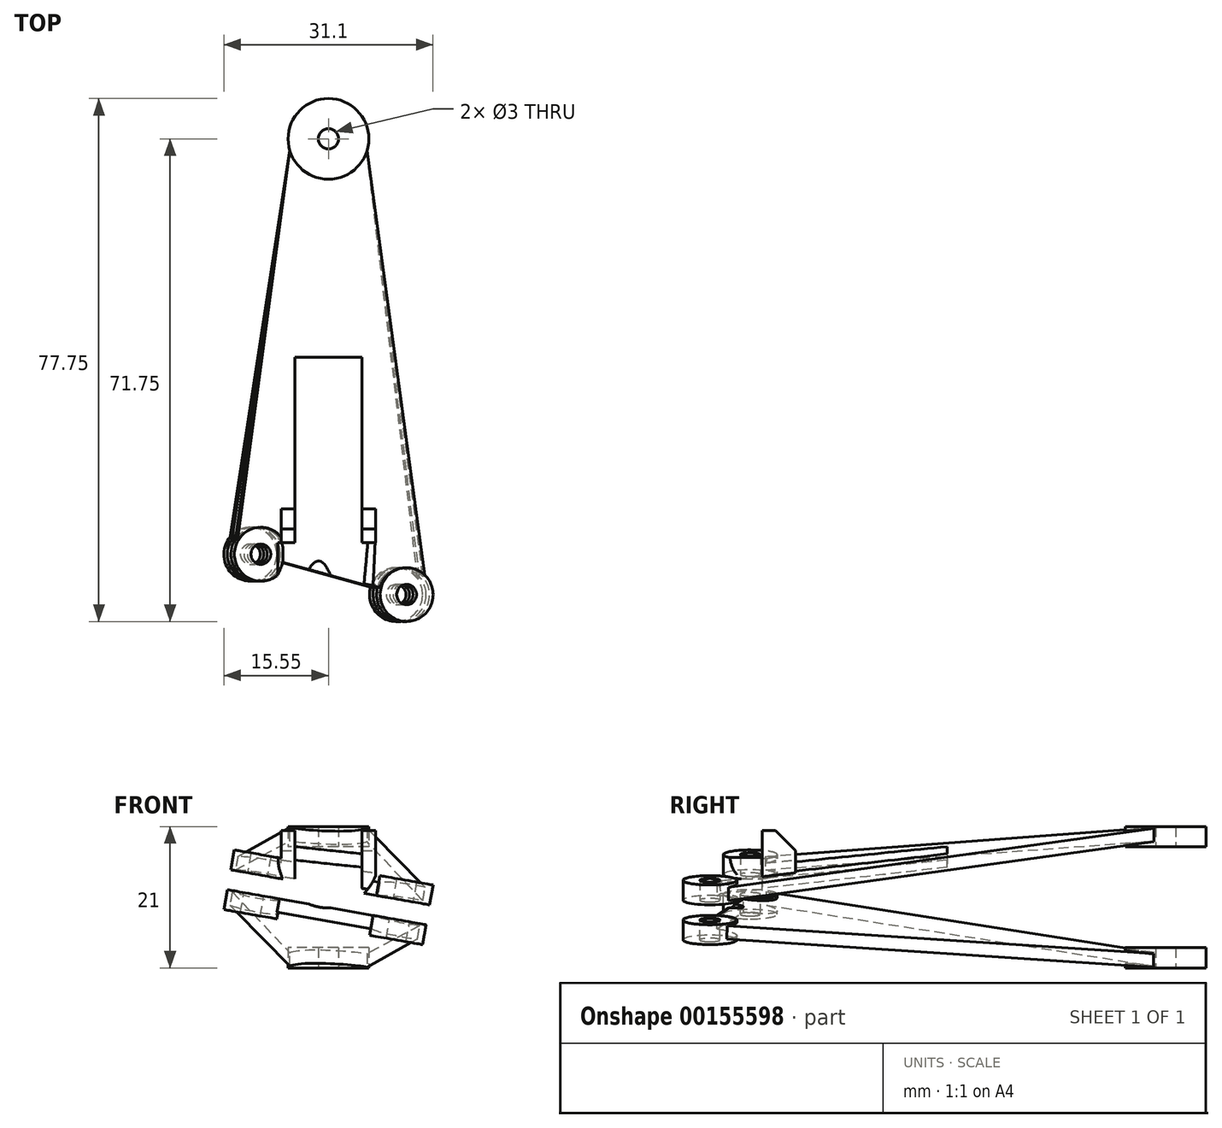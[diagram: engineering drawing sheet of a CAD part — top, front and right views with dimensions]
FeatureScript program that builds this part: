
annotation { "Feature Type Name" : "Feature", "Feature Type Description" : "" }
export const myFeature = defineFeature(function(context is Context, id is Id, definition is map)
    precondition{}
    {
        {
            var Q0;
            Q0=qCreatedBy(makeId("Front.planeOp"),FACE);
            var sketch = newSketch(context, id + "F0", { "sketchPlane" : qUnion([Q0])});
            skLineSegment(sketch, "E0", {"start": v(0, 0) * mm, "end": v(1.04, 5.9) * mm});
            skCircle(sketch, "E1", {"center": v(1.04, 5.9) * mm, "radius": 6 * mm});
            skLineSegment(sketch, "E2", {"start": v(0, 0) * mm, "end": v(-15.76, 2.78) * mm});
            skLineSegment(sketch, "E3", {"start": v(0, 0) * mm, "end": v(15.76, -2.78) * mm});
            skLineSegment(sketch, "E4", {"start": v(-10.83, 1.91) * mm, "end": v(-10.57, 3.39) * mm});
            skLineSegment(sketch, "E5", {"start": v(10.83, -1.91) * mm, "end": v(11.1, -0.43) * mm});
            skLineSegment(sketch, "E6", {"start": v(-10.83, 1.91) * mm, "end": v(-11.1, 0.43) * mm});
            skLineSegment(sketch, "E7", {"start": v(10.83, -1.91) * mm, "end": v(10.57, -3.39) * mm});
            skLineSegment(sketch, "E8", {"start": v(-5.9, 1.04) * mm, "end": v(-5.65, 2.52) * mm});
            skLineSegment(sketch, "E9", {"start": v(5.9, -1.04) * mm, "end": v(6.17, 0.44) * mm});
            skLineSegment(sketch, "E10", {"start": v(-5.9, 1.04) * mm, "end": v(-6.17, -0.44) * mm});
            skLineSegment(sketch, "E11", {"start": v(5.9, -1.04) * mm, "end": v(5.65, -2.52) * mm});
            skLineSegment(sketch, "E12.bottom", {"start": v(-10, 7.5) * mm, "end": v(10, 7.5) * mm});
            skLineSegment(sketch, "E12.top", {"start": v(-10, -7.5) * mm, "end": v(10, -7.5) * mm});
            skLineSegment(sketch, "E12.left", {"start": v(-10, 7.5) * mm, "end": v(-10, -7.5) * mm});
            skLineSegment(sketch, "E12.right", {"start": v(10, 7.5) * mm, "end": v(10, -7.5) * mm});
            skLineSegment(sketch, "E13", {"start": v(-9.5, -5.75) * mm, "end": v(9.5, -5.75) * mm});
            skLineSegment(sketch, "E14", {"start": v(-9.5, -3) * mm, "end": v(9.5, -3) * mm});
            skLineSegment(sketch, "E15", {"start": v(-9.5, 3) * mm, "end": v(9.5, 3) * mm});
            skLineSegment(sketch, "E16", {"start": v(-9.5, 5.75) * mm, "end": v(9.5, 5.75) * mm});
            skLineSegment(sketch, "E17", {"start": v(9.5, 7.5) * mm, "end": v(9.5, -7.5) * mm});
            skLineSegment(sketch, "E18", {"start": v(-9.5, 7.5) * mm, "end": v(-9.5, -7.5) * mm});
            skPoint(sketch, "E19.orphan", {"position": v(10, 5.75) * mm});
            skPoint(sketch, "E20.orphan", {"position": v(10, 3) * mm});
            skPoint(sketch, "E21.orphan", {"position": v(10, -3) * mm});
            skPoint(sketch, "E22.orphan", {"position": v(10, -5.75) * mm});
            skLineSegment(sketch, "E23", {"start": v(0, 7.5) * mm, "end": v(0, -7.5) * mm});
            skSolve(sketch);
        }
        {
            var Q0;
            {var subQ0=sQuery(id+"F0.wireOp",EDGE,"E12.bottom");var subQ1=sQuery(id+"F0.wireOp",EDGE,"E1");var subQ2=makeQuery(id+"F0.imprint","INTERSECT",VERTEX,{"disambiguationData":[OD(0.0)],"derivedFrom":[subQ1,subQ0]});Q0=makeQuery(id+"F0.imprint","IMPRINT",FACE,{"disambiguationData":[TD([[makeQuery(id+"F0.imprint","IMPRINT",EDGE,{"disambiguationData":[TD([[subQ2,1.0]])],"derivedFrom":subQ1}),1.0]])]});}
            cPlane(context, id + "F1", {"entities" : qUnion([Q0]), "cplaneType" : CPlaneType.OFFSET, "offset" : 1.75 * mm, "width" : 150 * mm, "height" : 150 * mm});
        }
        {
            var Q0;
            Q0=qCreatedBy(id+"F1.planeOp",FACE);
            var sketch = newSketch(context, id + "F2", { "sketchPlane" : qUnion([Q0])});
            skLineSegment(sketch, "E24", {"start": v(0, 0) * mm, "end": v(-10.83, 1.91) * mm});
            skLineSegment(sketch, "E25", {"start": v(-10.83, 1.91) * mm, "end": v(-10.05, 6.34) * mm});
            skSolve(sketch);
        }
        {
            var Q0;
            {var subQ0=sQuery(id+"F0.wireOp",EDGE,"E12.bottom");var subQ1=sQuery(id+"F0.wireOp",EDGE,"E1");var subQ2=makeQuery(id+"F0.imprint","INTERSECT",VERTEX,{"disambiguationData":[OD(0.0)],"derivedFrom":[subQ1,subQ0]});Q0=makeQuery(id+"F0.imprint","IMPRINT",FACE,{"disambiguationData":[TD([[makeQuery(id+"F0.imprint","IMPRINT",EDGE,{"disambiguationData":[TD([[subQ2,1.0]])],"derivedFrom":subQ1}),1.0]])]});}
            cPlane(context, id + "F3", {"entities" : qUnion([Q0]), "cplaneType" : CPlaneType.OFFSET, "offset" : 7.75 * mm, "width" : 150 * mm, "height" : 150 * mm});
        }
        {
            var Q0;
            Q0=qCreatedBy(id+"F3.planeOp",FACE);
            var sketch = newSketch(context, id + "F4", { "sketchPlane" : qUnion([Q0])});
            skLineSegment(sketch, "E26", {"start": v(0, 0) * mm, "end": v(10.83, -1.91) * mm});
            skLineSegment(sketch, "E27", {"start": v(10.83, -1.91) * mm, "end": v(11.61, 2.52) * mm});
            skSolve(sketch);
        }
        {
            var Q0;
            Q0=sQuery(id+"F0.wireOp",VERTEX,"E4.end");
            var Q1;
            Q1=sQuery(id+"F0.wireOp",EDGE,"E4");
            cPlane(context, id + "F5", {"entities" : qUnion([Q0, Q1]), "cplaneType" : CPlaneType.LINE_POINT, "offset" : 25 * mm, "width" : 150 * mm, "height" : 150 * mm});
        }
        {
            var Q0;
            Q0=qCreatedBy(id+"F5.planeOp",FACE);
            var sketch = newSketch(context, id + "F6", { "sketchPlane" : qUnion([Q0])});
            skCircle(sketch, "E28", {"center": v(-11, -1.75) * mm, "radius": 1.5 * mm});
            skCircle(sketch, "E29", {"center": v(-11, -1.75) * mm, "radius": 4 * mm});
            skCircle(sketch, "E30", {"center": v(11, -7.75) * mm, "radius": 1.5 * mm});
            skCircle(sketch, "E31", {"center": v(11, -7.75) * mm, "radius": 4 * mm});
            skLineSegment(sketch, "E32", {"start": v(-11, -1.75) * mm, "end": v(0, -1.75) * mm});
            skLineSegment(sketch, "E33", {"start": v(0, -1.75) * mm, "end": v(0, 0) * mm});
            skLineSegment(sketch, "E34", {"start": v(0, -1.75) * mm, "end": v(0, -7.75) * mm});
            skLineSegment(sketch, "E35", {"start": v(0, -7.75) * mm, "end": v(11, -7.75) * mm});
            skSolve(sketch);
        }
        {
            var Q0;
            Q0 = qSketchRegion(id + "F6", true);
            extrude(context, id + "F7", {"entities" : qUnion([Q0]), "depth" : 3 * mm});
        }
        {
            var Q0;
            Q0=qCreatedBy(makeId("Top.planeOp"),FACE);
            var sketch = newSketch(context, id + "F8", { "sketchPlane" : qUnion([Q0])});
            skLineSegment(sketch, "E36", {"start": v(0, 0) * mm, "end": v(0, 60) * mm});
            skCircle(sketch, "E37", {"center": v(0, 60) * mm, "radius": 6 * mm});
            skCircle(sketch, "E38", {"center": v(0, 60) * mm, "radius": 1.5 * mm});
            skSolve(sketch);
        }
        {
            var Q0;
            Q0=makeQuery(id+"F8.imprint","IMPRINT",FACE,{"disambiguationData":[TD([[makeQuery(id+"F8.imprint","IMPRINT",EDGE,{"derivedFrom":sQuery(id+"F8.wireOp",EDGE,"E37")}),1.0]])]});
            extrude(context, id + "F9", {"entities" : qUnion([Q0]), "depth" : 10.5 * mm, "hasSecondDirection" : true, "secondDirectionOppositeDirection" : true, "secondDirectionDepth" : 10.5 * mm});
        }
        {
            var Q0;
            Q0=makeQuery(id+"F8.imprint","IMPRINT",FACE,{"disambiguationData":[TD([[makeQuery(id+"F8.imprint","IMPRINT",EDGE,{"derivedFrom":sQuery(id+"F8.wireOp",EDGE,"E37")}),1.0]])]});
            extrude(context, id + "F10", {"entities" : qUnion([Q0]), "operationType" : NewBodyOperationType.REMOVE, "depth" : 7.5 * mm, "hasSecondDirection" : true, "secondDirectionOppositeDirection" : true, "secondDirectionDepth" : 7.5 * mm});
        }
        {
            var Q0;
            Q0=qCreatedBy(makeId("Right.planeOp"),FACE);
            var sketch = newSketch(context, id + "F11", { "sketchPlane" : qUnion([Q0])});
            skLineSegment(sketch, "E39", {"start": v(0, 5.9) * mm, "end": v(1.5, 5.9) * mm});
            skLineSegment(sketch, "E40", {"start": v(1.5, 5.9) * mm, "end": v(10.5, 5.9) * mm});
            skLineSegment(sketch, "E41", {"start": v(10.5, 5.9) * mm, "end": v(25.5, 5.9) * mm});
            skLineSegment(sketch, "E42", {"start": v(25.5, 5.9) * mm, "end": v(27.5, 5.9) * mm});
            skLineSegment(sketch, "E43.bottom", {"start": v(1.5, -0.1) * mm, "end": v(27.5, -0.1) * mm});
            skLineSegment(sketch, "E43.top", {"start": v(1.5, 11.9) * mm, "end": v(27.5, 11.9) * mm});
            skLineSegment(sketch, "E43.left", {"start": v(1.5, -0.1) * mm, "end": v(1.5, 11.9) * mm});
            skLineSegment(sketch, "E43.right", {"start": v(27.5, -0.1) * mm, "end": v(27.5, 11.9) * mm});
            skSolve(sketch);
        }
        {
            var Q0;
            Q0=qCreatedBy(makeId("Front.planeOp"),FACE);
            var sketch = newSketch(context, id + "F12", { "sketchPlane" : qUnion([Q0])});
            skLineSegment(sketch, "E44.bottom", {"start": v(-5, 11.9) * mm, "end": v(5, 11.9) * mm});
            skLineSegment(sketch, "E44.top", {"start": v(-5, -0.1) * mm, "end": v(5, -0.1) * mm});
            skLineSegment(sketch, "E44.left", {"start": v(-5, 11.9) * mm, "end": v(-5, -0.1) * mm});
            skLineSegment(sketch, "E44.right", {"start": v(5, 11.9) * mm, "end": v(5, -0.1) * mm});
            skCircle(sketch, "E45", {"center": v(0, 5.9) * mm, "radius": 2 * mm});
            skCircle(sketch, "E46", {"center": v(0, 10.4) * mm, "radius": 0.8 * mm});
            skCircle(sketch, "E47", {"center": v(0, 1.4) * mm, "radius": 0.8 * mm});
            skLineSegment(sketch, "E48.bottom", {"start": v(-5, 3.9) * mm, "end": v(-7, 3.9) * mm});
            skLineSegment(sketch, "E48.top", {"start": v(-5, 9.9) * mm, "end": v(-7, 9.9) * mm});
            skLineSegment(sketch, "E48.left", {"start": v(-5, 3.9) * mm, "end": v(-5, 9.9) * mm});
            skLineSegment(sketch, "E48.right", {"start": v(-7, 3.9) * mm, "end": v(-7, 9.9) * mm});
            skLineSegment(sketch, "E49.bottom", {"start": v(5, 9.9) * mm, "end": v(7, 9.9) * mm});
            skLineSegment(sketch, "E49.top", {"start": v(5, 1.9) * mm, "end": v(7, 1.9) * mm});
            skLineSegment(sketch, "E49.left", {"start": v(5, 9.9) * mm, "end": v(5, 1.9) * mm});
            skLineSegment(sketch, "E49.right", {"start": v(7, 9.9) * mm, "end": v(7, 1.9) * mm});
            skSolve(sketch);
        }
        {
            var Q0;
            Q0=makeQuery(id+"F12.imprint","IMPRINT",FACE,{"disambiguationData":[TD([[makeQuery(id+"F12.imprint","IMPRINT",EDGE,{"derivedFrom":sQuery(id+"F12.wireOp",EDGE,"E44.bottom")}),-1.0]])]});
            extrude(context, id + "F13", {"entities" : qUnion([Q0]), "oppositeDirection" : true, "depth" : 1.5 * mm});
        }
        {
            var Q0;
            Q0=makeQuery(id+"F13.opExtrude","CAP_EDGE",EDGE,{"disambiguationData":[OSD([sQuery(id+"F12.wireOp",EDGE,"E47")])],"isStart":true});
            var Q1;
            Q1=makeQuery(id+"F13.opExtrude","CAP_EDGE",EDGE,{"disambiguationData":[OSD([sQuery(id+"F12.wireOp",EDGE,"E46")])],"isStart":true});
            chamfer(context, id + "F14", {"entities" : qUnion([Q0, Q1]), "width" : .35 * mm, "tangentPropagation" : true});
        }
        {
            var Q0;
            Q0=sQuery(id+"F2.wireOp",VERTEX,"E25.end");
            var Q1;
            Q1=sQuery(id+"F2.wireOp",VERTEX,"E25.start");
            var Q2;
            Q2=sQuery(id+"F4.wireOp",VERTEX,"E27.end");
            cPlane(context, id + "F15", {"entities" : qUnion([Q0, Q1, Q2]), "cplaneType" : CPlaneType.THREE_POINT, "offset" : 25 * mm, "width" : 150 * mm, "height" : 150 * mm});
        }
        {
            var Q0;
            Q0=qCreatedBy(id+"F15.planeOp",FACE);
            var sketch = newSketch(context, id + "F16", { "sketchPlane" : qUnion([Q0])});
            skLineSegment(sketch, "E50", {"start": v(12.9, 5.92) * mm, "end": v(-16.61, 0.52) * mm});
            skLineSegment(sketch, "E51", {"start": v(-16.61, 0.52) * mm, "end": v(-16.25, -1.45) * mm});
            skLineSegment(sketch, "E52", {"start": v(-16.25, -1.45) * mm, "end": v(13.26, 3.95) * mm});
            skLineSegment(sketch, "E53", {"start": v(13.26, 3.95) * mm, "end": v(12.9, 5.92) * mm});
            skLineSegment(sketch, "E54", {"start": v(13.8, 1) * mm, "end": v(-15.72, -4.4) * mm});
            skLineSegment(sketch, "E55", {"start": v(-15.72, -4.4) * mm, "end": v(-15.36, -6.36) * mm});
            skLineSegment(sketch, "E56", {"start": v(-15.36, -6.36) * mm, "end": v(14.16, -0.97) * mm});
            skLineSegment(sketch, "E57", {"start": v(14.16, -0.97) * mm, "end": v(13.8, 1) * mm});
            skSolve(sketch);
        }
        {
            var Q0;
            Q0=qCreatedBy(makeId("Front.planeOp"),FACE);
            var Q1;
            Q1=sQuery(id+"F8.wireOp",VERTEX,"E38.center");
            cPlane(context, id + "F17", {"entities" : qUnion([Q0, Q1]), "cplaneType" : CPlaneType.PLANE_POINT, "offset" : 25 * mm, "width" : 150 * mm, "height" : 150 * mm});
        }
        {
            var Q0;
            Q0=qCreatedBy(id+"F17.planeOp",FACE);
            var sketch = newSketch(context, id + "F18", { "sketchPlane" : qUnion([Q0])});
            skLineSegment(sketch, "E58.bottom", {"start": v(-5.5, 10.5) * mm, "end": v(5.5, 10.5) * mm});
            skLineSegment(sketch, "E58.top", {"start": v(-5.5, 8.5) * mm, "end": v(5.5, 8.5) * mm});
            skLineSegment(sketch, "E58.left", {"start": v(-5.5, 10.5) * mm, "end": v(-5.5, 8.5) * mm});
            skLineSegment(sketch, "E58.right", {"start": v(5.5, 10.5) * mm, "end": v(5.5, 8.5) * mm});
            skLineSegment(sketch, "E59.MirrorCS", {"start": v(-5.5, -10.5) * mm, "end": v(-5.5, -8.5) * mm});
            skLineSegment(sketch, "E60.MirrorCS", {"start": v(-5.5, -10.5) * mm, "end": v(5.5, -10.5) * mm});
            skLineSegment(sketch, "E61.MirrorCS", {"start": v(-5.5, -8.5) * mm, "end": v(5.5, -8.5) * mm});
            skLineSegment(sketch, "E62.MirrorCS", {"start": v(5.5, -10.5) * mm, "end": v(5.5, -8.5) * mm});
            skSolve(sketch);
        }
        {
            var Q3;
            Q3=makeQuery(id+"F16.imprint","IMPRINT",FACE,{"disambiguationData":[TD([[makeQuery(id+"F16.imprint","IMPRINT",EDGE,{"derivedFrom":sQuery(id+"F16.wireOp",EDGE,"E50")}),1.0]])]});
            var Q4;
            Q4=makeQuery(id+"F18.imprint","IMPRINT",FACE,{"disambiguationData":[TD([[makeQuery(id+"F18.imprint","IMPRINT",EDGE,{"derivedFrom":sQuery(id+"F18.wireOp",EDGE,"E58.bottom")}),-1.0]])]});
            loft(context, id + "F19", {"operationType" : NewBodyOperationType.ADD, "sheetProfilesArray" : [{ "sheetProfileEntities" : qUnion([Q3]) }, { "sheetProfileEntities" : qUnion([Q4]) }]});
        }
        {
            var Q0;
            Q0=makeQuery(id+"F6.imprint","IMPRINT",FACE,{"disambiguationData":[TD([[makeQuery(id+"F6.imprint","IMPRINT",EDGE,{"derivedFrom":sQuery(id+"F6.wireOp",EDGE,"E28")}),1.0]])]});
            var Q1;
            Q1=makeQuery(id+"F6.imprint","IMPRINT",FACE,{"disambiguationData":[TD([[makeQuery(id+"F6.imprint","IMPRINT",EDGE,{"derivedFrom":sQuery(id+"F6.wireOp",EDGE,"E30")}),1.0]])]});
            extrude(context, id + "F20", {"entities" : qUnion([Q0, Q1]), "operationType" : NewBodyOperationType.REMOVE, "depth" : 25 * mm});
        }
        {
            var Q0;
            Q0=makeQuery(id+"F8.imprint","IMPRINT",FACE,{"disambiguationData":[TD([[makeQuery(id+"F8.imprint","IMPRINT",EDGE,{"derivedFrom":sQuery(id+"F8.wireOp",EDGE,"E38")}),1.0]])]});
            var Q1;
            Q1=sQuery(id+"F8.wireOp",EDGE,"E38");
            extrude(context, id + "F21", {"entities" : qUnion([Q0]), "operationType" : NewBodyOperationType.REMOVE, "surfaceEntities" : qUnion([Q1]), "depth" : 25 * mm});
        }
        {
            var Q0;
            Q0=qCreatedBy(id+"F5.planeOp",FACE);
            var Q1;
            Q1=sQuery(id+"F0.wireOp",VERTEX,"E6.end");
            cPlane(context, id + "F22", {"entities" : qUnion([Q0, Q1]), "cplaneType" : CPlaneType.PLANE_POINT, "offset" : 25 * mm, "width" : 150 * mm, "height" : 150 * mm});
        }
        {
            var Q0;
            Q0=qCreatedBy(id+"F22.planeOp",FACE);
            var sketch = newSketch(context, id + "F23", { "sketchPlane" : qUnion([Q0])});
            skCircle(sketch, "E63", {"center": v(-11, -1.75) * mm, "radius": 1.5 * mm});
            skCircle(sketch, "E64", {"center": v(-11, -1.75) * mm, "radius": 4 * mm});
            skCircle(sketch, "E65", {"center": v(11, -7.75) * mm, "radius": 1.5 * mm});
            skCircle(sketch, "E66", {"center": v(11, -7.75) * mm, "radius": 4 * mm});
            skSolve(sketch);
        }
        {
            var Q1;
            Q1=makeQuery(id+"F16.imprint","IMPRINT",FACE,{"disambiguationData":[TD([[makeQuery(id+"F16.imprint","IMPRINT",EDGE,{"derivedFrom":sQuery(id+"F16.wireOp",EDGE,"E54")}),1.0]])]});
            var Q2;
            Q2=makeQuery(id+"F18.imprint","IMPRINT",FACE,{"disambiguationData":[TD([[makeQuery(id+"F18.imprint","IMPRINT",EDGE,{"derivedFrom":sQuery(id+"F18.wireOp",EDGE,"E59.MirrorCS")}),-1.0]])]});
            loft(context, id + "F24", {"operationType" : NewBodyOperationType.ADD, "sheetProfilesArray" : [{ "sheetProfileEntities" : qUnion([Q1]) }, { "sheetProfileEntities" : qUnion([Q2]) }]});
        }
        {
            var Q0;
            Q0=makeQuery(id+"F23.imprint","IMPRINT",FACE,{"disambiguationData":[TD([[makeQuery(id+"F23.imprint","IMPRINT",EDGE,{"derivedFrom":sQuery(id+"F23.wireOp",EDGE,"E63")}),-1.0]])]});
            var Q1;
            Q1=makeQuery(id+"F23.imprint","IMPRINT",FACE,{"disambiguationData":[TD([[makeQuery(id+"F23.imprint","IMPRINT",EDGE,{"derivedFrom":sQuery(id+"F23.wireOp",EDGE,"E65")}),-1.0]])]});
            extrude(context, id + "F25", {"entities" : qUnion([Q0, Q1]), "operationType" : NewBodyOperationType.ADD, "oppositeDirection" : true, "depth" : 3 * mm});
        }
        {
            var Q0;
            Q0=makeQuery(id+"F23.imprint","IMPRINT",FACE,{"disambiguationData":[TD([[makeQuery(id+"F23.imprint","IMPRINT",EDGE,{"derivedFrom":sQuery(id+"F23.wireOp",EDGE,"E63")}),1.0]])]});
            var Q1;
            Q1=makeQuery(id+"F23.imprint","IMPRINT",FACE,{"disambiguationData":[TD([[makeQuery(id+"F23.imprint","IMPRINT",EDGE,{"derivedFrom":sQuery(id+"F23.wireOp",EDGE,"E65")}),1.0]])]});
            extrude(context, id + "F26", {"entities" : qUnion([Q0, Q1]), "operationType" : NewBodyOperationType.REMOVE, "oppositeDirection" : true, "depth" : 25 * mm});
        }
        {
            var Q0;
            Q0=makeQuery(id+"F8.imprint","IMPRINT",FACE,{"disambiguationData":[TD([[makeQuery(id+"F8.imprint","IMPRINT",EDGE,{"derivedFrom":sQuery(id+"F8.wireOp",EDGE,"E38")}),1.0]])]});
            extrude(context, id + "F27", {"entities" : qUnion([Q0]), "operationType" : NewBodyOperationType.REMOVE, "oppositeDirection" : true, "depth" : 25 * mm});
        }
        {
            var Q0;
            Q0=makeQuery(id+"F12.imprint","IMPRINT",FACE,{"disambiguationData":[TD([[makeQuery(id+"F12.imprint","IMPRINT",EDGE,{"derivedFrom":sQuery(id+"F12.wireOp",EDGE,"E45")}),1.0]])]});
            var Q1;
            Q1=makeQuery(id+"F12.imprint","IMPRINT",FACE,{"disambiguationData":[TD([[makeQuery(id+"F12.imprint","IMPRINT",EDGE,{"derivedFrom":sQuery(id+"F12.wireOp",EDGE,"E46")}),1.0]])]});
            var Q2;
            Q2=makeQuery(id+"F12.imprint","IMPRINT",FACE,{"disambiguationData":[TD([[makeQuery(id+"F12.imprint","IMPRINT",EDGE,{"derivedFrom":sQuery(id+"F12.wireOp",EDGE,"E44.bottom")}),-1.0]])]});
            var Q3;
            Q3=makeQuery(id+"F12.imprint","IMPRINT",FACE,{"disambiguationData":[TD([[makeQuery(id+"F12.imprint","IMPRINT",EDGE,{"derivedFrom":sQuery(id+"F12.wireOp",EDGE,"E47")}),1.0]])]});
            extrude(context, id + "F28", {"entities" : qUnion([Q0, Q1, Q2, Q3]), "operationType" : NewBodyOperationType.REMOVE, "oppositeDirection" : true, "depth" : 27.5 * mm});
        }
        {
            var Q0;
            Q0=makeQuery(id+"F12.imprint","IMPRINT",FACE,{"disambiguationData":[TD([[makeQuery(id+"F12.imprint","IMPRINT",EDGE,{"derivedFrom":sQuery(id+"F12.wireOp",EDGE,"E48.bottom")}),-1.0]])]});
            var Q1;
            Q1=makeQuery(id+"F12.imprint","IMPRINT",FACE,{"disambiguationData":[TD([[makeQuery(id+"F12.imprint","IMPRINT",EDGE,{"derivedFrom":sQuery(id+"F12.wireOp",EDGE,"E49.bottom")}),-1.0]])]});
            extrude(context, id + "F29", {"entities" : qUnion([Q0, Q1]), "operationType" : NewBodyOperationType.ADD, "oppositeDirection" : true, "depth" : 5 * mm});
        }
        {
            var Q0;
            Q0=makeQuery(id+"F29.opExtrude","CAP_EDGE",EDGE,{"disambiguationData":[OSD([sQuery(id+"F12.wireOp",EDGE,"E48.top")])],"isStart":false});
            var Q1;
            Q1=makeQuery(id+"F29.opExtrude","CAP_EDGE",EDGE,{"disambiguationData":[OSD([sQuery(id+"F12.wireOp",EDGE,"E49.bottom")])],"isStart":false});
            chamfer(context, id + "F30", {"entities" : qUnion([Q0, Q1]), "width" : 3 * mm, "tangentPropagation" : true});
        }
        {
            var Q0;
            Q0=qCreatedBy(makeId("Front.planeOp"),FACE);
            var sketch = newSketch(context, id + "F31", { "sketchPlane" : qUnion([Q0])});
            skCircle(sketch, "E67", {"center": v(0, 5.9) * mm, "radius": 7.5 * mm});
            skSolve(sketch);
        }
        {
            var Q0;
            Q0 = qSketchRegion(id + "F31", true);
            extrude(context, id + "F32", {"entities" : qUnion([Q0]), "operationType" : NewBodyOperationType.REMOVE, "depth" : 25 * mm});
        }
    });
